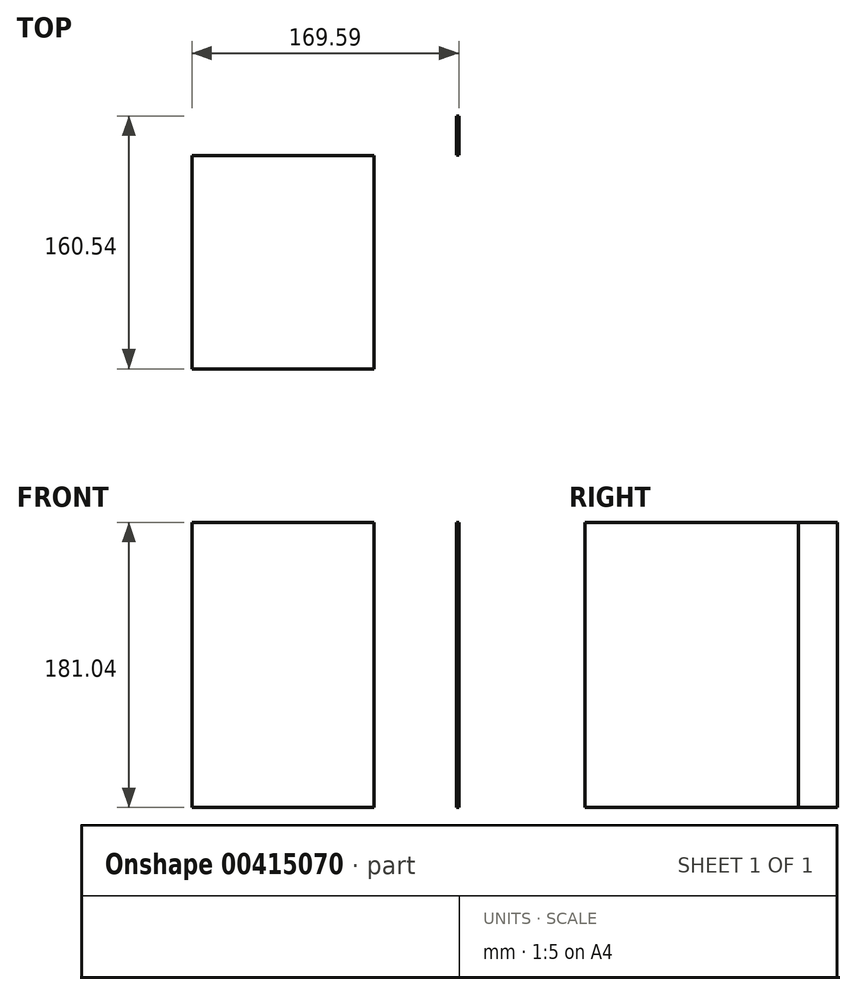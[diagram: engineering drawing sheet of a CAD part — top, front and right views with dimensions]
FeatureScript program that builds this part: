
annotation { "Feature Type Name" : "Feature", "Feature Type Description" : "" }
export const myFeature = defineFeature(function(context is Context, id is Id, definition is map)
    precondition{}
    {
        {
            var Q0;
            Q0=qCreatedBy(makeId("Top.planeOp"),FACE);
            var sketch = newSketch(context, id + "F0", { "sketchPlane" : qUnion([Q0])});
            skLineSegment(sketch, "E0.bottom", {"start": v(0, 24.54) * mm, "end": v(0, 24.54) * mm});
            skLineSegment(sketch, "E0.top", {"start": v(0, 0) * mm, "end": v(0, 0) * mm});
            skLineSegment(sketch, "E0.left", {"start": v(0, 24.54) * mm, "end": v(0, 0) * mm});
            skLineSegment(sketch, "E0.right", {"start": v(0, 24.54) * mm, "end": v(0, 0) * mm});
            skLineSegment(sketch, "E1.bottom", {"start": v(54.2, 71.8) * mm, "end": v(-61.34, 71.8) * mm});
            skLineSegment(sketch, "E1.top", {"start": v(54.2, -63.83) * mm, "end": v(-61.34, -63.83) * mm});
            skLineSegment(sketch, "E1.left", {"start": v(54.2, 71.8) * mm, "end": v(54.2, -63.83) * mm});
            skLineSegment(sketch, "E1.right", {"start": v(-61.34, 71.8) * mm, "end": v(-61.34, -63.83) * mm});
            skLineSegment(sketch, "E2.bottom", {"start": v(0, 24.54) * mm, "end": v(39.33, 24.54) * mm});
            skLineSegment(sketch, "E2.top", {"start": v(0, 71.8) * mm, "end": v(39.33, 71.8) * mm});
            skLineSegment(sketch, "E2.left", {"start": v(0, 24.54) * mm, "end": v(0, 71.8) * mm});
            skLineSegment(sketch, "E2.right", {"start": v(39.33, 24.54) * mm, "end": v(39.33, 71.8) * mm});
            skLineSegment(sketch, "E3.bottom", {"start": v(108.25, 96.7) * mm, "end": v(106.8, 96.7) * mm});
            skLineSegment(sketch, "E3.top", {"start": v(108.25, 71.86) * mm, "end": v(106.8, 71.86) * mm});
            skLineSegment(sketch, "E3.left", {"start": v(108.25, 96.7) * mm, "end": v(108.25, 71.86) * mm});
            skLineSegment(sketch, "E3.right", {"start": v(106.8, 96.7) * mm, "end": v(106.8, 71.86) * mm});
            skLineSegment(sketch, "E4.bottom", {"start": v(19.67, 24.54) * mm, "end": v(150.7, 24.54) * mm, "construction": true});
            skLineSegment(sketch, "E4.top", {"start": v(19.67, 86.05) * mm, "end": v(150.7, 86.05) * mm, "construction": true});
            skLineSegment(sketch, "E4.left", {"start": v(19.67, 24.54) * mm, "end": v(19.67, 86.05) * mm, "construction": true});
            skLineSegment(sketch, "E4.right", {"start": v(150.7, 24.54) * mm, "end": v(150.7, 86.05) * mm, "construction": true});
            skSolve(sketch);
        }
        {
            var Q0;
            Q0 = qSketchRegion(id + "F0", true);
            extrude(context, id + "F1", {"entities" : qUnion([Q0]), "depth" : 181.04 * mm});
        }
    });
